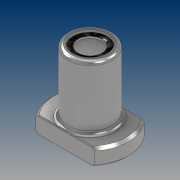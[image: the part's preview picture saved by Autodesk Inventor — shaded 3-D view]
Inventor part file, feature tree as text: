
AUTODESK INVENTOR PART (.ipt)
format: ipt  version: 2021 (Build 250183000, 183)  size: 204,288 bytes
history: native  units: mm
features: extrude x4, sketch x3, fillet x2, plane x2, chamfer x2, projected_geometry x1
ambient origin geometry x8: Origin, YZ Plane, XZ Plane, XY Plane, X Axis, Y Axis, Z Axis, Center Point
bodies: Solid1 (feature_tree)
feature tree (14):
  sketch  "Sketch1"  dims[d0=29.0mm d1=45.0mm]
  extrude  "Extrusion1"  Depth=29.0mm
  extrude  "Extrusion2"  Depth=10.0mm
  fillet  "Fillet1"  Radius=10.0mm
  plane  "Work Plane1"
  extrude  "Extrusion3"  Depth=2.0mm
  plane  "Work Plane2"
  extrude  "Extrusion4"  [1 undecoded]
  chamfer  "Chamfer1"  Distance=14.0mm
  chamfer  "Chamfer2"  Distance=1.25mm
  fillet  "Fillet2"  [1 undecoded]
  sketch  "Sketch2"  dims[d2=20.0mm d3=26.0mm d4=10.0mm d5=0.0mm]
  sketch  "Sketch3"  dims[d6=37.0mm d7=0.0mm d8=2.0mm d9=-3.0mm d10=14.0mm d11=1.25mm d12=0.0mm d13=-1.25mm d14=14.0mm d15=1.0mm d16=0.0mm d17=0.5mm d18=2.0mm d19=45.0deg d20=1.5mm d21=2.0mm d22=45.0deg d23=2.0mm]
  projected_geometry  "Projected Loop1"
note: 2 required parameter values undecoded (feature->parameter linkage not recoverable at this tier; creation-order binding heuristic only, values carry confidence <= 0.55)
